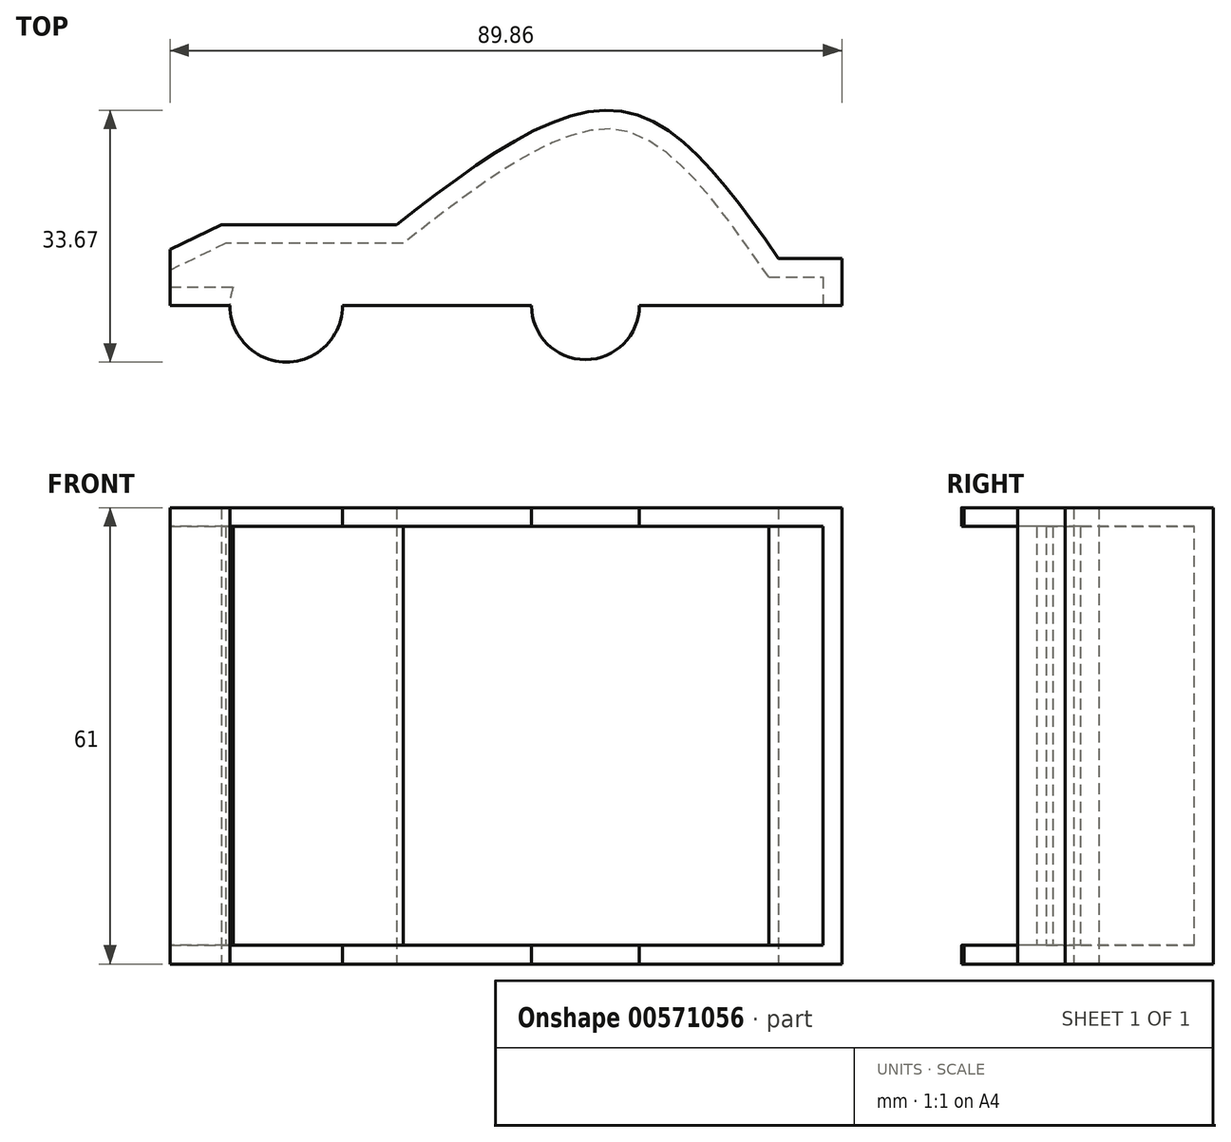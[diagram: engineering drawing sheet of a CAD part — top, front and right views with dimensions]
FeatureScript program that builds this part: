
annotation { "Feature Type Name" : "Feature", "Feature Type Description" : "" }
export const myFeature = defineFeature(function(context is Context, id is Id, definition is map)
    precondition{}
    {
        {
            var Q0;
            Q0=qCreatedBy(makeId("Top.planeOp"),FACE);
            var sketch = newSketch(context, id + "F0", { "sketchPlane" : qUnion([Q0])});
            skFitSpline(sketch, "E0", {"points": [v(25.82, 11.04) * mm, v(4.73, 30.74) * mm, v(-25.22, 15.57) * mm], "startDerivative": vector(-40.49, 57.85) * mm, "endDerivative": vector(-61.33, -47.46) * mm});
            skLineSegment(sketch, "E1", {"start": v(-25.22, 15.57) * mm, "end": v(-48.68, 15.57) * mm});
            skLineSegment(sketch, "E2", {"start": v(-48.68, 15.57) * mm, "end": v(-55.57, 12.22) * mm});
            skLineSegment(sketch, "E3", {"start": v(-55.57, 12.22) * mm, "end": v(-55.57, 4.73) * mm});
            skCircle(sketch, "E4", {"center": v(-40, 4.73) * mm, "radius": 7.53 * mm});
            skLineSegment(sketch, "E5", {"start": v(-55.57, 4.73) * mm, "end": v(-47.53, 4.73) * mm});
            skLineSegment(sketch, "E6", {"start": v(-32.48, 4.74) * mm, "end": v(-11.44, 4.74) * mm});
            skCircle(sketch, "E7", {"center": v(0, 4.74) * mm, "radius": 7.22 * mm});
            skLineSegment(sketch, "E8", {"start": v(-11.44, 4.74) * mm, "end": v(-7.22, 4.74) * mm});
            skLineSegment(sketch, "E9", {"start": v(25.82, 11.04) * mm, "end": v(34.3, 11.04) * mm});
            skLineSegment(sketch, "E10", {"start": v(34.3, 11.04) * mm, "end": v(34.3, 4.74) * mm});
            skLineSegment(sketch, "E11", {"start": v(34.3, 4.74) * mm, "end": v(7.22, 4.74) * mm});
            skSolve(sketch);
        }
        {
            var Q0;
            {var subQ0=sQuery(id+"F0.wireOp",EDGE,"E4");var subQ1=makeQuery(id+"F0.imprint","INTERSECT",VERTEX,{"derivedFrom":[subQ0,sQuery(id+"F0.wireOp",EDGE,"E5")]});Q0=makeQuery(id+"F0.imprint","IMPRINT",FACE,{"disambiguationData":[TD([[makeQuery(id+"F0.imprint","IMPRINT",EDGE,{"disambiguationData":[TD([[subQ1,1.0]])],"derivedFrom":subQ0}),1.0]])]});}
            var Q1;
            {var subQ0=sQuery(id+"F0.wireOp",EDGE,"E7");var subQ1=makeQuery(id+"F0.imprint","INTERSECT",VERTEX,{"derivedFrom":[subQ0,sQuery(id+"F0.wireOp",EDGE,"E8")]});Q1=makeQuery(id+"F0.imprint","IMPRINT",FACE,{"disambiguationData":[TD([[makeQuery(id+"F0.imprint","IMPRINT",EDGE,{"disambiguationData":[TD([[subQ1,1.0]])],"derivedFrom":subQ0}),1.0]])]});}
            var Q2;
            Q2=makeQuery(id+"F0.imprint","IMPRINT",FACE,{"disambiguationData":[TD([[makeQuery(id+"F0.imprint","IMPRINT",EDGE,{"derivedFrom":sQuery(id+"F0.wireOp",EDGE,"E0")}),1.0]])]});
            extrude(context, id + "F1", {"entities" : qUnion([Q0, Q1, Q2]), "endBound" : BoundingType.SYMMETRIC, "depth" : 3 * mm, "offsetDistance" : 25.4 * mm});
        }
        {
            var Q0;
            Q0=makeQuery(id+"F1.opExtrude","CAP_FACE",FACE,{"disambiguationData":[OSD([sQuery(id+"F0.wireOp",EDGE,"E0"),sQuery(id+"F0.wireOp",EDGE,"E1"),sQuery(id+"F0.wireOp",EDGE,"E2"),sQuery(id+"F0.wireOp",EDGE,"E3"),sQuery(id+"F0.wireOp",EDGE,"E4"),sQuery(id+"F0.wireOp",EDGE,"E5"),sQuery(id+"F0.wireOp",EDGE,"E6"),sQuery(id+"F0.wireOp",EDGE,"E7"),sQuery(id+"F0.wireOp",EDGE,"E8"),sQuery(id+"F0.wireOp",EDGE,"E9"),sQuery(id+"F0.wireOp",EDGE,"E10"),sQuery(id+"F0.wireOp",EDGE,"E11")])],"isStart":false});
            extrude(context, id + "F2", {"entities" : qUnion([Q0]), "operationType" : NewBodyOperationType.ADD, "depth" : 58 * mm, "offsetDistance" : 25.4 * mm});
        }
        {
            var Q0;
            {var subQ0=sQuery(id+"F0.wireOp",EDGE,"E8");var subQ1=sQuery(id+"F0.wireOp",EDGE,"E6");Q0=makeQuery(id+"F2.boolean.opBoolean","MERGE",FACE,{"derivedFrom":[makeQuery(id+"F1.opExtrude","SWEPT_FACE",FACE,{"disambiguationData":[OSD([subQ1,subQ0])]}),makeQuery(id+"F2.opExtrude","SWEPT_FACE",FACE,{"disambiguationData":[OSD([subQ1,subQ0])]})]});}
            var Q1;
            {var subQ0=sQuery(id+"F0.wireOp",EDGE,"E7");Q1=makeQuery(id+"F2.boolean.opBoolean","MERGE",FACE,{"derivedFrom":[makeQuery(id+"F1.opExtrude","SWEPT_FACE",FACE,{"disambiguationData":[OSD([subQ0])]}),makeQuery(id+"F2.opExtrude","SWEPT_FACE",FACE,{"disambiguationData":[OSD([subQ0])]})]});}
            var Q2;
            {var subQ0=sQuery(id+"F0.wireOp",EDGE,"E11");Q2=makeQuery(id+"F2.boolean.opBoolean","MERGE",FACE,{"derivedFrom":[makeQuery(id+"F1.opExtrude","SWEPT_FACE",FACE,{"disambiguationData":[OSD([subQ0])]}),makeQuery(id+"F2.opExtrude","SWEPT_FACE",FACE,{"disambiguationData":[OSD([subQ0])]})]});}
            var Q3;
            {var subQ0=sQuery(id+"F0.wireOp",EDGE,"E3");Q3=makeQuery(id+"F2.boolean.opBoolean","MERGE",FACE,{"derivedFrom":[makeQuery(id+"F1.opExtrude","SWEPT_FACE",FACE,{"disambiguationData":[OSD([subQ0])]}),makeQuery(id+"F2.opExtrude","SWEPT_FACE",FACE,{"disambiguationData":[OSD([subQ0])]})]});}
            var Q4;
            {var subQ0=sQuery(id+"F0.wireOp",EDGE,"E4");Q4=makeQuery(id+"F2.boolean.opBoolean","MERGE",FACE,{"derivedFrom":[makeQuery(id+"F1.opExtrude","SWEPT_FACE",FACE,{"disambiguationData":[OSD([subQ0])]}),makeQuery(id+"F2.opExtrude","SWEPT_FACE",FACE,{"disambiguationData":[OSD([subQ0])]})]});}
            shell(context, id + "F3", {"entities" : qUnion([Q0, Q1, Q2, Q3, Q4]), "thickness" : 2.5 * mm});
        }
    });
